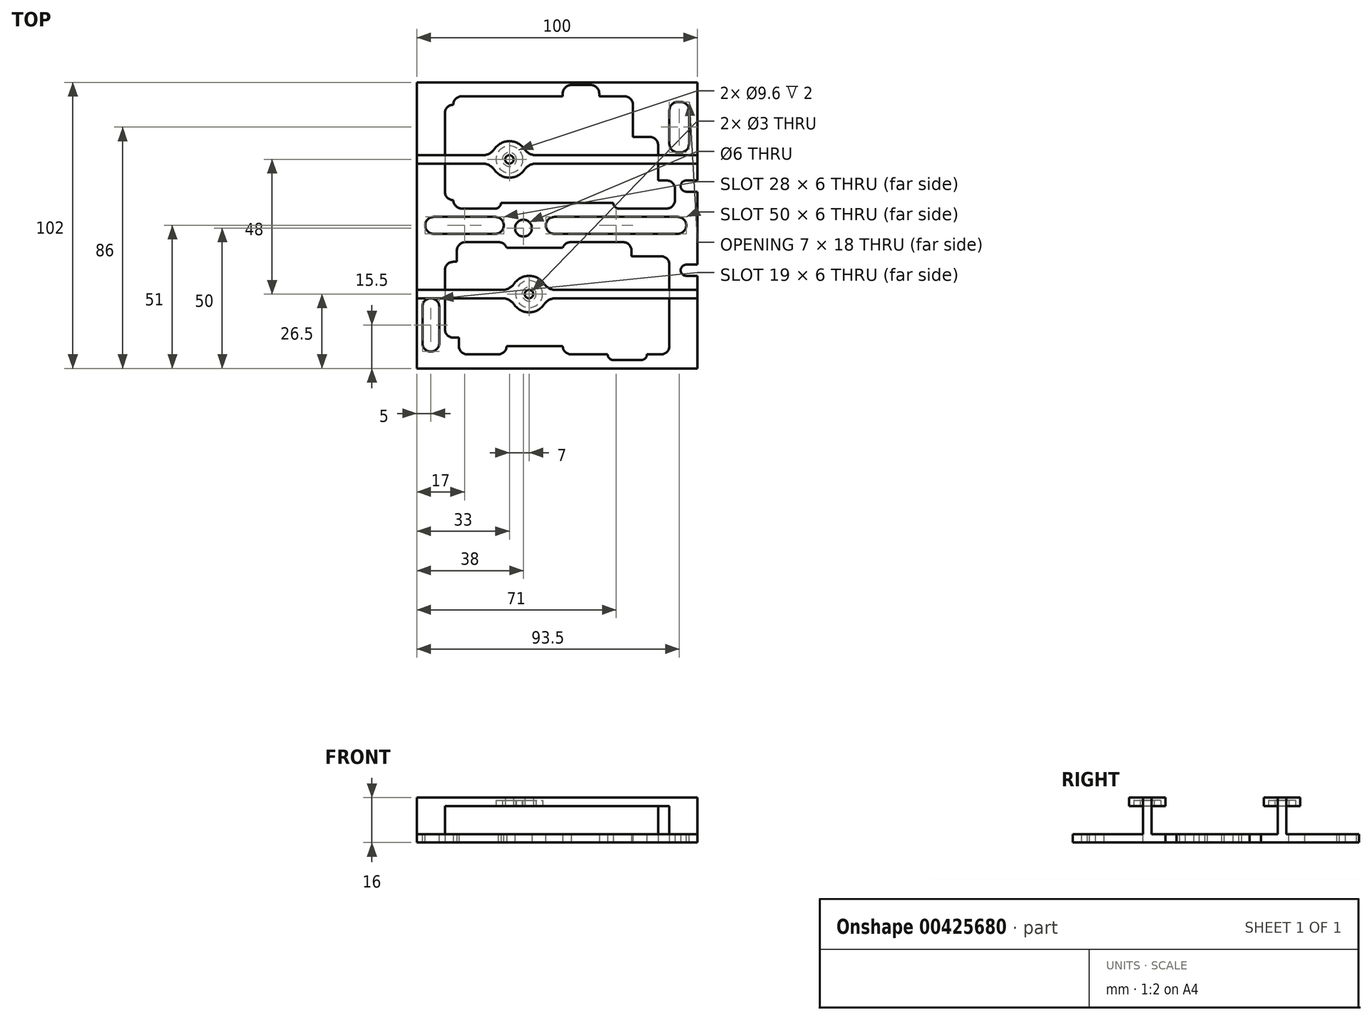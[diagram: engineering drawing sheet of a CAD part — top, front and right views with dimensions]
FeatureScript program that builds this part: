
annotation { "Feature Type Name" : "Feature", "Feature Type Description" : "" }
export const myFeature = defineFeature(function(context is Context, id is Id, definition is map)
    precondition{}
    {
        {
            var Q0;
            Q0=qCreatedBy(makeId("Top.planeOp"),FACE);
            var sketch = newSketch(context, id + "F0", { "sketchPlane" : qUnion([Q0])});
            skLineSegment(sketch, "E0.bottom", {"start": v(3, 0) * mm, "end": v(97, 0) * mm});
            skLineSegment(sketch, "E0.top", {"start": v(3, 102) * mm, "end": v(97, 102) * mm});
            skLineSegment(sketch, "E0.left", {"start": v(0, 0) * mm, "end": v(0, 102) * mm});
            skLineSegment(sketch, "E0.right", {"start": v(100, 0) * mm, "end": v(100, 33) * mm});
            skLineSegment(sketch, "E1.bottom", {"start": v(26, 97) * mm, "end": v(52, 97) * mm});
            skLineSegment(sketch, "E1.top", {"start": v(23, 57) * mm, "end": v(28, 57) * mm});
            skLineSegment(sketch, "E1.left", {"start": v(10, 91) * mm, "end": v(10, 63) * mm});
            skLineSegment(sketch, "E1.right", {"start": v(86, 79.5) * mm, "end": v(86, 67) * mm});
            skLineSegment(sketch, "E2.left", {"start": v(10, 35) * mm, "end": v(10, 14) * mm});
            skLineSegment(sketch, "E3.top", {"start": v(77, 82.5) * mm, "end": v(83, 82.5) * mm});
            skLineSegment(sketch, "E3.left", {"start": v(77, 88.5) * mm, "end": v(77, 82.5) * mm});
            skPoint(sketch, "E4.orphan", {"position": v(91.75, 82.5) * mm});
            skLineSegment(sketch, "E5.bottom", {"start": v(55, 101) * mm, "end": v(62, 101) * mm});
            skLineSegment(sketch, "E5.left", {"start": v(52, 98) * mm, "end": v(52, 97) * mm});
            skLineSegment(sketch, "E5.right", {"start": v(65, 98) * mm, "end": v(65, 97) * mm});
            skLineSegment(sketch, "E6.trimOffspring", {"start": v(65, 97) * mm, "end": v(74, 97) * mm});
            skLineSegment(sketch, "E7", {"start": v(72, 57) * mm, "end": v(89, 57) * mm});
            skLineSegment(sketch, "E8", {"start": v(86, 67) * mm, "end": v(89, 67) * mm});
            skLineSegment(sketch, "E9", {"start": v(92, 60) * mm, "end": v(92, 64) * mm});
            skLineSegment(sketch, "E10.top", {"start": v(14.3, 38) * mm, "end": v(13, 38) * mm});
            skLineSegment(sketch, "E11.bottom", {"start": v(13, 11) * mm, "end": v(15, 11) * mm});
            skLineSegment(sketch, "E12.trimOffspring", {"start": v(26, 45) * mm, "end": v(29.34, 45) * mm});
            skLineSegment(sketch, "E13.trimOffspring", {"start": v(24, 5) * mm, "end": v(29, 5) * mm});
            skLineSegment(sketch, "E14.right", {"start": v(90, 35.75) * mm, "end": v(90, 16.5) * mm});
            skLineSegment(sketch, "E15.top", {"start": v(70, 3) * mm, "end": v(80, 3) * mm});
            skLineSegment(sketch, "E16.trimOffspring", {"start": v(82, 5) * mm, "end": v(87, 5) * mm});
            skLineSegment(sketch, "E17", {"start": v(11.68, 51) * mm, "end": v(-20.94, 51) * mm, "construction": true});
            skCircle(sketch, "E18", {"center": v(38, 50) * mm, "radius": 3 * mm});
            skLineSegment(sketch, "E19", {"start": v(77, 88.5) * mm, "end": v(77, 94) * mm});
            skLineSegment(sketch, "E20", {"start": v(13, 94) * mm, "end": v(13, 94) * mm});
            skLineSegment(sketch, "E21", {"start": v(13, 60) * mm, "end": v(13, 60) * mm});
            skLineSegment(sketch, "E22", {"start": v(30, 59) * mm, "end": v(30, 59) * mm});
            skLineSegment(sketch, "E23", {"start": v(70, 59) * mm, "end": v(70, 59) * mm});
            skLineSegment(sketch, "E24", {"start": v(30, 59) * mm, "end": v(70, 59) * mm});
            skLineSegment(sketch, "E25", {"start": v(90, 16.5) * mm, "end": v(90, 8) * mm});
            skLineSegment(sketch, "E26", {"start": v(76.5, 42) * mm, "end": v(76.5, 40) * mm});
            skLineSegment(sketch, "E27", {"start": v(76.5, 40) * mm, "end": v(76.5, 40) * mm});
            skLineSegment(sketch, "E28.top", {"start": v(32, 8) * mm, "end": v(52, 8) * mm});
            skLineSegment(sketch, "E28.left", {"start": v(32, 8) * mm, "end": v(32, 8) * mm});
            skLineSegment(sketch, "E28.right", {"start": v(52, 8) * mm, "end": v(52, 8) * mm});
            skLineSegment(sketch, "E29.top", {"start": v(32, 43) * mm, "end": v(52, 43) * mm});
            skLineSegment(sketch, "E30.trimOffspring", {"start": v(55, 5) * mm, "end": v(68, 5) * mm});
            skLineSegment(sketch, "E31.trimOffspring", {"start": v(55, 45) * mm, "end": v(73.5, 45) * mm});
            skLineSegment(sketch, "E32", {"start": v(3, 0) * mm, "end": v(0, 0) * mm});
            skLineSegment(sketch, "E33", {"start": v(97, 0) * mm, "end": v(100, 0) * mm});
            skLineSegment(sketch, "E34", {"start": v(3, 102) * mm, "end": v(0, 102) * mm});
            skLineSegment(sketch, "E35", {"start": v(97, 102) * mm, "end": v(100, 102) * mm});
            skPoint(sketch, "E36.MirrorCS.start.orphan", {"position": v(100, 102) * mm});
            skLineSegment(sketch, "E37", {"start": v(26, 45) * mm, "end": v(17.3, 45) * mm});
            skLineSegment(sketch, "E38", {"start": v(14.3, 42) * mm, "end": v(14.3, 38) * mm});
            skArc(sketch, "E39.filletArc", {"start": v(17.3, 45) * mm, "mid": v(15.18, 44.12) * mm, "end": v(14.3, 42) * mm});
            skPoint(sketch, "E40.visualSharp", {"position": v(10, 38) * mm});
            skArc(sketch, "E40.filletArc", {"start": v(13, 38) * mm, "mid": v(10.88, 37.12) * mm, "end": v(10, 35) * mm});
            skPoint(sketch, "E41.visualSharp", {"position": v(10, 11) * mm});
            skArc(sketch, "E41.filletArc", {"start": v(10, 14) * mm, "mid": v(10.88, 11.88) * mm, "end": v(13, 11) * mm});
            skArc(sketch, "E42.filletArc", {"start": v(76.5, 42) * mm, "mid": v(75.62, 44.12) * mm, "end": v(73.5, 45) * mm});
            skLineSegment(sketch, "E43", {"start": v(76.5, 40) * mm, "end": v(87, 40) * mm});
            skLineSegment(sketch, "E44", {"start": v(90, 37) * mm, "end": v(90, 35.75) * mm});
            skPoint(sketch, "E45.visualSharp", {"position": v(90, 40) * mm});
            skArc(sketch, "E45.filletArc", {"start": v(90, 37) * mm, "mid": v(89.12, 39.12) * mm, "end": v(87, 40) * mm});
            skPoint(sketch, "E46.visualSharp", {"position": v(90, 5) * mm});
            skArc(sketch, "E46.filletArc", {"start": v(87, 5) * mm, "mid": v(89.12, 5.88) * mm, "end": v(90, 8) * mm});
            skPoint(sketch, "E47.visualSharp", {"position": v(52, 5) * mm});
            skArc(sketch, "E47.filletArc", {"start": v(52, 8) * mm, "mid": v(52.88, 5.88) * mm, "end": v(55, 5) * mm});
            skPoint(sketch, "E48.visualSharp", {"position": v(32, 5) * mm});
            skArc(sketch, "E48.filletArc", {"start": v(29, 5) * mm, "mid": v(31.12, 5.88) * mm, "end": v(32, 8) * mm});
            skArc(sketch, "E49", {"start": v(32, 43) * mm, "mid": v(30.83, 44.5) * mm, "end": v(29, 45) * mm});
            skPoint(sketch, "E29.left.start.orphan", {"position": v(32, 45) * mm});
            skArc(sketch, "E50", {"start": v(55, 45) * mm, "mid": v(53.17, 44.5) * mm, "end": v(52, 43) * mm});
            skArc(sketch, "E51", {"start": v(68, 5) * mm, "mid": v(68.59, 3.59) * mm, "end": v(70, 3) * mm});
            skArc(sketch, "E52", {"start": v(80, 3) * mm, "mid": v(81.41, 3.59) * mm, "end": v(82, 5) * mm});
            skLineSegment(sketch, "E53", {"start": v(18, 5) * mm, "end": v(24, 5) * mm});
            skLineSegment(sketch, "E54", {"start": v(15, 11) * mm, "end": v(15, 8) * mm});
            skPoint(sketch, "E55.visualSharp", {"position": v(15, 5) * mm});
            skArc(sketch, "E55.filletArc", {"start": v(15, 8) * mm, "mid": v(15.88, 5.88) * mm, "end": v(18, 5) * mm});
            skPoint(sketch, "E56.visualSharp", {"position": v(52, 101) * mm});
            skArc(sketch, "E56.filletArc", {"start": v(55, 101) * mm, "mid": v(52.88, 100.12) * mm, "end": v(52, 98) * mm});
            skPoint(sketch, "E57.visualSharp", {"position": v(65, 101) * mm});
            skArc(sketch, "E57.filletArc", {"start": v(65, 98) * mm, "mid": v(64.12, 100.12) * mm, "end": v(62, 101) * mm});
            skPoint(sketch, "E58.visualSharp", {"position": v(77, 97) * mm});
            skArc(sketch, "E58.filletArc", {"start": v(77, 94) * mm, "mid": v(76.12, 96.12) * mm, "end": v(74, 97) * mm});
            skPoint(sketch, "E59.visualSharp", {"position": v(86, 82.5) * mm});
            skArc(sketch, "E59.filletArc", {"start": v(86, 79.5) * mm, "mid": v(85.12, 81.62) * mm, "end": v(83, 82.5) * mm});
            skPoint(sketch, "E60.visualSharp", {"position": v(92, 67) * mm});
            skArc(sketch, "E60.filletArc", {"start": v(92, 64) * mm, "mid": v(91.12, 66.12) * mm, "end": v(89, 67) * mm});
            skPoint(sketch, "E61.visualSharp", {"position": v(92, 57) * mm});
            skArc(sketch, "E61.filletArc", {"start": v(89, 57) * mm, "mid": v(91.12, 57.88) * mm, "end": v(92, 60) * mm});
            skPoint(sketch, "E62.visualSharp", {"position": v(30, 57) * mm});
            skArc(sketch, "E62.filletArc", {"start": v(28, 57) * mm, "mid": v(29.41, 57.59) * mm, "end": v(30, 59) * mm});
            skPoint(sketch, "E63.visualSharp", {"position": v(70, 57) * mm});
            skArc(sketch, "E63.filletArc", {"start": v(70, 59) * mm, "mid": v(70.59, 57.59) * mm, "end": v(72, 57) * mm});
            skLineSegment(sketch, "E64", {"start": v(26, 97) * mm, "end": v(16, 97) * mm});
            skPoint(sketch, "E65.newPointA", {"position": v(13, 96.86) * mm});
            skPoint(sketch, "E65.newPointB", {"position": v(13, 97) * mm});
            skArc(sketch, "E65.filletArc", {"start": v(16, 97) * mm, "mid": v(13.88, 96.12) * mm, "end": v(13, 94) * mm});
            skPoint(sketch, "E66.visualSharp", {"position": v(10, 94) * mm});
            skArc(sketch, "E66.filletArc", {"start": v(13, 94) * mm, "mid": v(10.88, 93.12) * mm, "end": v(10, 91) * mm});
            skLineSegment(sketch, "E67", {"start": v(23, 57) * mm, "end": v(16, 57) * mm});
            skPoint(sketch, "E68.visualSharp", {"position": v(10, 60) * mm});
            skArc(sketch, "E68.filletArc", {"start": v(10, 63) * mm, "mid": v(10.88, 60.88) * mm, "end": v(13, 60) * mm});
            skPoint(sketch, "E69.visualSharp", {"position": v(13, 57) * mm});
            skArc(sketch, "E69.filletArc", {"start": v(13, 60) * mm, "mid": v(13.88, 57.88) * mm, "end": v(16, 57) * mm});
            skArc(sketch, "E70", {"start": v(96, 37) * mm, "mid": v(94, 35) * mm, "end": v(96, 33) * mm});
            skArc(sketch, "E71", {"start": v(96, 67) * mm, "mid": v(94, 65) * mm, "end": v(96, 63) * mm});
            skLineSegment(sketch, "E72", {"start": v(96, 67) * mm, "end": v(100, 67) * mm});
            skLineSegment(sketch, "E73", {"start": v(96, 63) * mm, "end": v(100, 63) * mm});
            skLineSegment(sketch, "E74.trimOffspring", {"start": v(100, 67) * mm, "end": v(100, 102) * mm});
            skLineSegment(sketch, "E75.bottom", {"start": v(96, 37) * mm, "end": v(100, 37) * mm});
            skLineSegment(sketch, "E76.bottom", {"start": v(96, 33) * mm, "end": v(100, 33) * mm});
            skLineSegment(sketch, "E77.trimOffspring", {"start": v(100, 37) * mm, "end": v(100, 63) * mm});
            skSolve(sketch);
        }
        {
            var Q0;
            Q0=qSketchRegion(id+"F0",true);
            extrude(context, id + "F1", {"entities" : qUnion([Q0]), "depth" : 3 * mm, "offsetDistance" : 25 * mm});
        }
        {
            var Q0;
            Q0=makeQuery(id+"F1.opExtrude","CAP_FACE",FACE,{"disambiguationData":[OSD([sQuery(id+"F0.wireOp",EDGE,"E0.bottom"),sQuery(id+"F0.wireOp",EDGE,"E0.top"),sQuery(id+"F0.wireOp",EDGE,"E0.left"),sQuery(id+"F0.wireOp",EDGE,"E0.right"),sQuery(id+"F0.wireOp",EDGE,"E1.bottom"),sQuery(id+"F0.wireOp",EDGE,"E1.top"),sQuery(id+"F0.wireOp",EDGE,"E1.left"),sQuery(id+"F0.wireOp",EDGE,"E1.right"),sQuery(id+"F0.wireOp",EDGE,"E2.left"),sQuery(id+"F0.wireOp",EDGE,"E2.right"),sQuery(id+"F0.wireOp",EDGE,"E3.top"),sQuery(id+"F0.wireOp",EDGE,"E3.left"),sQuery(id+"F0.wireOp",EDGE,"E5.bottom"),sQuery(id+"F0.wireOp",EDGE,"E5.left"),sQuery(id+"F0.wireOp",EDGE,"E5.right"),sQuery(id+"F0.wireOp",EDGE,"E6.trimOffspring"),sQuery(id+"F0.wireOp",EDGE,"OxCn24rm-5nCi-klrK-E0W5-i8LOYMI6os4h.bottom"),sQuery(id+"F0.wireOp",EDGE,"OxCn24rm-5nCi-klrK-E0W5-i8LOYMI6os4h.right"),sQuery(id+"F0.wireOp",EDGE,"rXKhr1xD-5eTB-sLtH-Qrwl-SqILkHBMoKIC.top"),sQuery(id+"F0.wireOp",EDGE,"rXKhr1xD-5eTB-sLtH-Qrwl-SqILkHBMoKIC.right"),sQuery(id+"F0.wireOp",EDGE,"wjIKWsUY-1y7m-uhNO-1cWs-wJh5i1SVGTS4"),sQuery(id+"F0.wireOp",EDGE,"Fd2FQQkF-qeS2-SP9m-kDKw-uxav5DLLBaqb"),sQuery(id+"F0.wireOp",EDGE,"ZQqpw7ko-XBrV-Zwog-WddX-ZsBwI7n4kIzG"),sQuery(id+"F0.wireOp",EDGE,"E7"),sQuery(id+"F0.wireOp",EDGE,"E8"),sQuery(id+"F0.wireOp",EDGE,"E9"),sQuery(id+"F0.wireOp",EDGE,"ORbpDnOW-ThUp-Z5K2-SE26-eshPCraVd0tb.top"),sQuery(id+"F0.wireOp",EDGE,"ORbpDnOW-ThUp-Z5K2-SE26-eshPCraVd0tb.left"),sQuery(id+"F0.wireOp",EDGE,"E10.top"),sQuery(id+"F0.wireOp",EDGE,"E10.left"),sQuery(id+"F0.wireOp",EDGE,"dN3iFH4H-qRAM-YeRZ-ol0c-A4IXgtGxA8XV.top"),sQuery(id+"F0.wireOp",EDGE,"dN3iFH4H-qRAM-YeRZ-ol0c-A4IXgtGxA8XV.left"),sQuery(id+"F0.wireOp",EDGE,"E11.bottom"),sQuery(id+"F0.wireOp",EDGE,"E11.right"),sQuery(id+"F0.wireOp",EDGE,"E12.trimOffspring"),sQuery(id+"F0.wireOp",EDGE,"E13.trimOffspring"),sQuery(id+"F0.wireOp",EDGE,"bjdKxRGc-RBqR-6Ud0-CWuA-04plJlh88Ydx.top"),sQuery(id+"F0.wireOp",EDGE,"bjdKxRGc-RBqR-6Ud0-CWuA-04plJlh88Ydx.left"),sQuery(id+"F0.wireOp",EDGE,"E14.right"),sQuery(id+"F0.wireOp",EDGE,"2f8da56e-dfad-408c-ba04-36b25fe1f5d9.trimOffspring"),sQuery(id+"F0.wireOp",EDGE,"E15.top"),sQuery(id+"F0.wireOp",EDGE,"E15.left"),sQuery(id+"F0.wireOp",EDGE,"E15.right"),sQuery(id+"F0.wireOp",EDGE,"E16.trimOffspring"),sQuery(id+"F0.wireOp",EDGE,"A49D6E9r-1JUr-9GDP-vNaZ-ViviVAoOX606"),sQuery(id+"F0.wireOp",EDGE,"vtlNYRCa-Do6P-C0d5-ElFE-HTToTMsx1Fji"),sQuery(id+"F0.wireOp",EDGE,"lmL8inpJ-ytwe-dLrc-ad7L-TpwxuQ8vTU9b"),sQuery(id+"F0.wireOp",EDGE,"h73Oo6xC-rRRI-xAcJ-BuA6-SMJPpPIosUSZ"),sQuery(id+"F0.wireOp",EDGE,"au1NNZ2t-6lUs-IFa9-xlba-gWE9ZIKOgp08"),sQuery(id+"F0.wireOp",EDGE,"yvoELJC3-YjSa-WHdH-b68Q-IG7KWKIGRjHb"),sQuery(id+"F0.wireOp",EDGE,"ERycc8vl-z3Cl-hGIG-RQzm-87voCwp2birA"),sQuery(id+"F0.wireOp",EDGE,"E2MXITla-3G0j-ucNW-0Zkd-STVuzueoCgdE.top"),sQuery(id+"F0.wireOp",EDGE,"E2MXITla-3G0j-ucNW-0Zkd-STVuzueoCgdE.left"),sQuery(id+"F0.wireOp",EDGE,"E2MXITla-3G0j-ucNW-0Zkd-STVuzueoCgdE.right"),sQuery(id+"F0.wireOp",EDGE,"Ca3rMzd9-FrgB-pphp-Oxqs-IZKiP3cJTDne"),sQuery(id+"F0.wireOp",EDGE,"7T3Rpf4S-CqYs-le4C-O5dJ-dI1EBJDtCbfp"),sQuery(id+"F0.wireOp",EDGE,"997c3999-b55e-490c-beb5-2bee1e2e1c940.MirrorCS"),sQuery(id+"F0.wireOp",EDGE,"c3554b98-e3f3-445f-801e-a0076f2162810.MirrorCS"),sQuery(id+"F0.wireOp",EDGE,"E36.MirrorCS"),sQuery(id+"F0.wireOp",EDGE,"4368e434-94b6-4df4-879f-dcd640d41f0e0.MirrorCS"),sQuery(id+"F0.wireOp",EDGE,"37798aaa-42c0-4cef-a439-54f5e668db9a0.MirrorCS"),sQuery(id+"F0.wireOp",EDGE,"d064ad95-df91-4078-a0f9-9f58f394fbd70.MirrorCS"),sQuery(id+"F0.wireOp",EDGE,"08820286-3d7b-404e-9f5a-cb54356c3d8d0.MirrorCS"),sQuery(id+"F0.wireOp",EDGE,"1518c572-78e2-41d5-bc5d-d8ca2dcde2710.MirrorCS"),sQuery(id+"F0.wireOp",EDGE,"E18"),sQuery(id+"F0.wireOp",EDGE,"DqYHB80w-fGch-NoDe-N2a7-YfNS9cl1PrHZ"),sQuery(id+"F0.wireOp",EDGE,"Tbt3sgnV-WqdU-Oisj-Q5Qw-zABe9o91ZCy5"),sQuery(id+"F0.wireOp",EDGE,"fXqGHVZl-Qcgk-zm2a-7tLV-AyFcCwGseMAn"),sQuery(id+"F0.wireOp",EDGE,"RIbojJIC-BDsi-60La-0oJR-OISrQjfgBfsT"),sQuery(id+"F0.wireOp",EDGE,"Y7Jcioam-hEoO-QEPg-HWFz-VR7Pjhn3heaJ"),sQuery(id+"F0.wireOp",EDGE,"PzUnhAa5-5pe3-GNiC-2A5K-FJAJxwR9T3X4"),sQuery(id+"F0.wireOp",EDGE,"rlzUklQd-3dkf-QKTa-yDw8-YwjNvcUjzYi0"),sQuery(id+"F0.wireOp",EDGE,"JA5SAORn-5zCI-tt9o-vuvb-NJhDItHEi9iq"),sQuery(id+"F0.wireOp",EDGE,"qvz8dSCR-gKGT-wn8P-gyaW-mG4SNKuXNP92"),sQuery(id+"F0.wireOp",EDGE,"Ehq0zpWA-Svbj-95kT-JLI7-XYxp3DV2qt0l")])],"isStart":false});
            var sketch = newSketch(context, id + "F2", { "sketchPlane" : qUnion([Q0])});
            skLineSegment(sketch, "E78.bottom", {"start": v(0, 25) * mm, "end": v(10, 25) * mm});
            skLineSegment(sketch, "E78.top", {"start": v(0, 28) * mm, "end": v(10, 28) * mm});
            skLineSegment(sketch, "E78.left", {"start": v(0, 25) * mm, "end": v(0, 28) * mm});
            skLineSegment(sketch, "E78.right", {"start": v(100, 25) * mm, "end": v(100, 28) * mm});
            skLineSegment(sketch, "E79.bottom", {"start": v(0, 73) * mm, "end": v(10, 73) * mm});
            skLineSegment(sketch, "E79.top", {"start": v(0, 76) * mm, "end": v(10, 76) * mm});
            skLineSegment(sketch, "E79.left", {"start": v(0, 73) * mm, "end": v(0, 76) * mm});
            skLineSegment(sketch, "E79.right", {"start": v(100, 73) * mm, "end": v(100, 76) * mm});
            skLineSegment(sketch, "E80", {"start": v(10, 73) * mm, "end": v(10, 76) * mm});
            skLineSegment(sketch, "E81", {"start": v(10, 28) * mm, "end": v(10, 25) * mm});
            skLineSegment(sketch, "E82", {"start": v(90, 28) * mm, "end": v(90, 25) * mm});
            skLineSegment(sketch, "E83", {"start": v(86, 76) * mm, "end": v(86, 73) * mm});
            skLineSegment(sketch, "E84.trimOffspring", {"start": v(90, 28) * mm, "end": v(100, 28) * mm});
            skLineSegment(sketch, "E85.trimOffspring", {"start": v(90, 25) * mm, "end": v(100, 25) * mm});
            skLineSegment(sketch, "E86.trimOffspring", {"start": v(86, 76) * mm, "end": v(100, 76) * mm});
            skLineSegment(sketch, "E87.trimOffspring", {"start": v(86, 73) * mm, "end": v(100, 73) * mm});
            skSolve(sketch);
        }
        {
            var Q0;
            Q0=qSketchRegion(id+"F2",true);
            extrude(context, id + "F3", {"entities" : qUnion([Q0]), "operationType" : NewBodyOperationType.ADD, "depth" : 10 * mm});
        }
        {
            var Q0;
            Q0=makeQuery(id+"F3.opExtrude","CAP_FACE",FACE,{"disambiguationData":[OSD([sQuery(id+"F2.wireOp",EDGE,"E78.bottom"),sQuery(id+"F2.wireOp",EDGE,"E78.top"),sQuery(id+"F2.wireOp",EDGE,"E78.left"),sQuery(id+"F2.wireOp",EDGE,"E81")])],"isStart":false});
            var sketch = newSketch(context, id + "F4", { "sketchPlane" : qUnion([Q0])});
            skLineSegment(sketch, "E88.0", {"start": v(0, 25) * mm, "end": v(0, 28) * mm});
            skLineSegment(sketch, "E89.0", {"start": v(100, 28) * mm, "end": v(100, 25) * mm});
            skLineSegment(sketch, "E90.0", {"start": v(100, 76) * mm, "end": v(100, 73) * mm});
            skLineSegment(sketch, "E91.0", {"start": v(0, 73) * mm, "end": v(0, 76) * mm});
            skLineSegment(sketch, "E92", {"start": v(0, 76) * mm, "end": v(26.68, 76) * mm});
            skLineSegment(sketch, "E93", {"start": v(0, 73) * mm, "end": v(26.68, 73) * mm});
            skLineSegment(sketch, "E94", {"start": v(0, 28) * mm, "end": v(33.68, 28) * mm});
            skLineSegment(sketch, "E95", {"start": v(0, 25) * mm, "end": v(33.68, 25) * mm});
            skArc(sketch, "E96", {"start": v(26.68, 73) * mm, "mid": v(33, 68) * mm, "end": v(39.32, 73) * mm});
            skArc(sketch, "E97", {"start": v(33.68, 25) * mm, "mid": v(40, 20) * mm, "end": v(46.32, 25) * mm});
            skLineSegment(sketch, "E98.trimOffspring", {"start": v(39.32, 73) * mm, "end": v(100, 73) * mm});
            skLineSegment(sketch, "E99.trimOffspring", {"start": v(39.32, 76) * mm, "end": v(100, 76) * mm});
            skArc(sketch, "E100.trimOffspring", {"start": v(39.32, 76) * mm, "mid": v(33, 81) * mm, "end": v(26.68, 76) * mm});
            skLineSegment(sketch, "E101.trimOffspring", {"start": v(46.32, 28) * mm, "end": v(100, 28) * mm});
            skLineSegment(sketch, "E102.trimOffspring", {"start": v(46.32, 25) * mm, "end": v(100, 25) * mm});
            skArc(sketch, "E103.trimOffspring", {"start": v(46.32, 28) * mm, "mid": v(40, 33) * mm, "end": v(33.68, 28) * mm});
            skSolve(sketch);
        }
        {
            var Q0;
            Q0 = qSketchRegion(id + "F4", true);
            extrude(context, id + "F5", {"entities" : qUnion([Q0]), "operationType" : NewBodyOperationType.ADD, "depth" : 3 * mm});
        }
        {
            var Q0;
            Q0=makeQuery(id+"F5.opExtrude","CAP_FACE",FACE,{"disambiguationData":[OSD([sQuery(id+"F4.wireOp",EDGE,"E88.0"),sQuery(id+"F4.wireOp",EDGE,"E89.0"),sQuery(id+"F4.wireOp",EDGE,"E94"),sQuery(id+"F4.wireOp",EDGE,"E95"),sQuery(id+"F4.wireOp",EDGE,"E97"),sQuery(id+"F4.wireOp",EDGE,"E101.trimOffspring"),sQuery(id+"F4.wireOp",EDGE,"E102.trimOffspring"),sQuery(id+"F4.wireOp",EDGE,"E103.trimOffspring")])],"isStart":true});
            var sketch = newSketch(context, id + "F6", { "sketchPlane" : qUnion([Q0])});
            skCircle(sketch, "E104", {"center": v(40, -26.5) * mm, "radius": 4.8 * mm});
            skCircle(sketch, "E105", {"center": v(33, -74.5) * mm, "radius": 4.8 * mm});
            skCircle(sketch, "E106", {"center": v(40, -26.5) * mm, "radius": 2.5 * mm});
            skCircle(sketch, "E107", {"center": v(33, -74.5) * mm, "radius": 2.5 * mm});
            skSolve(sketch);
        }
        {
            var Q0;
            Q0 = qSketchRegion(id + "F6", true);
            extrude(context, id + "F7", {"entities" : qUnion([Q0]), "operationType" : NewBodyOperationType.REMOVE, "oppositeDirection" : true, "depth" : 2 * mm});
        }
        {
            var Q0;
            Q0=makeQuery(id+"F1.opExtrude","CAP_FACE",FACE,{"disambiguationData":[OSD([sQuery(id+"F0.wireOp",EDGE,"E0.bottom"),sQuery(id+"F0.wireOp",EDGE,"E0.top"),sQuery(id+"F0.wireOp",EDGE,"E0.left"),sQuery(id+"F0.wireOp",EDGE,"E0.right"),sQuery(id+"F0.wireOp",EDGE,"E1.bottom"),sQuery(id+"F0.wireOp",EDGE,"E1.top"),sQuery(id+"F0.wireOp",EDGE,"E1.left"),sQuery(id+"F0.wireOp",EDGE,"E1.right"),sQuery(id+"F0.wireOp",EDGE,"E2.left"),sQuery(id+"F0.wireOp",EDGE,"E2.right"),sQuery(id+"F0.wireOp",EDGE,"E3.top"),sQuery(id+"F0.wireOp",EDGE,"E3.left"),sQuery(id+"F0.wireOp",EDGE,"E5.bottom"),sQuery(id+"F0.wireOp",EDGE,"E5.left"),sQuery(id+"F0.wireOp",EDGE,"E5.right"),sQuery(id+"F0.wireOp",EDGE,"E6.trimOffspring"),sQuery(id+"F0.wireOp",EDGE,"OxCn24rm-5nCi-klrK-E0W5-i8LOYMI6os4h.bottom"),sQuery(id+"F0.wireOp",EDGE,"OxCn24rm-5nCi-klrK-E0W5-i8LOYMI6os4h.right"),sQuery(id+"F0.wireOp",EDGE,"rXKhr1xD-5eTB-sLtH-Qrwl-SqILkHBMoKIC.top"),sQuery(id+"F0.wireOp",EDGE,"rXKhr1xD-5eTB-sLtH-Qrwl-SqILkHBMoKIC.right"),sQuery(id+"F0.wireOp",EDGE,"wjIKWsUY-1y7m-uhNO-1cWs-wJh5i1SVGTS4"),sQuery(id+"F0.wireOp",EDGE,"Fd2FQQkF-qeS2-SP9m-kDKw-uxav5DLLBaqb"),sQuery(id+"F0.wireOp",EDGE,"ZQqpw7ko-XBrV-Zwog-WddX-ZsBwI7n4kIzG"),sQuery(id+"F0.wireOp",EDGE,"E7"),sQuery(id+"F0.wireOp",EDGE,"E8"),sQuery(id+"F0.wireOp",EDGE,"E9"),sQuery(id+"F0.wireOp",EDGE,"ORbpDnOW-ThUp-Z5K2-SE26-eshPCraVd0tb.top"),sQuery(id+"F0.wireOp",EDGE,"ORbpDnOW-ThUp-Z5K2-SE26-eshPCraVd0tb.left"),sQuery(id+"F0.wireOp",EDGE,"E10.top"),sQuery(id+"F0.wireOp",EDGE,"E10.left"),sQuery(id+"F0.wireOp",EDGE,"dN3iFH4H-qRAM-YeRZ-ol0c-A4IXgtGxA8XV.top"),sQuery(id+"F0.wireOp",EDGE,"dN3iFH4H-qRAM-YeRZ-ol0c-A4IXgtGxA8XV.left"),sQuery(id+"F0.wireOp",EDGE,"E11.bottom"),sQuery(id+"F0.wireOp",EDGE,"E11.right"),sQuery(id+"F0.wireOp",EDGE,"E12.trimOffspring"),sQuery(id+"F0.wireOp",EDGE,"E13.trimOffspring"),sQuery(id+"F0.wireOp",EDGE,"bjdKxRGc-RBqR-6Ud0-CWuA-04plJlh88Ydx.top"),sQuery(id+"F0.wireOp",EDGE,"bjdKxRGc-RBqR-6Ud0-CWuA-04plJlh88Ydx.left"),sQuery(id+"F0.wireOp",EDGE,"E14.right"),sQuery(id+"F0.wireOp",EDGE,"2f8da56e-dfad-408c-ba04-36b25fe1f5d9.trimOffspring"),sQuery(id+"F0.wireOp",EDGE,"E15.top"),sQuery(id+"F0.wireOp",EDGE,"E15.left"),sQuery(id+"F0.wireOp",EDGE,"E15.right"),sQuery(id+"F0.wireOp",EDGE,"E16.trimOffspring"),sQuery(id+"F0.wireOp",EDGE,"A49D6E9r-1JUr-9GDP-vNaZ-ViviVAoOX606"),sQuery(id+"F0.wireOp",EDGE,"vtlNYRCa-Do6P-C0d5-ElFE-HTToTMsx1Fji"),sQuery(id+"F0.wireOp",EDGE,"lmL8inpJ-ytwe-dLrc-ad7L-TpwxuQ8vTU9b"),sQuery(id+"F0.wireOp",EDGE,"h73Oo6xC-rRRI-xAcJ-BuA6-SMJPpPIosUSZ"),sQuery(id+"F0.wireOp",EDGE,"au1NNZ2t-6lUs-IFa9-xlba-gWE9ZIKOgp08"),sQuery(id+"F0.wireOp",EDGE,"yvoELJC3-YjSa-WHdH-b68Q-IG7KWKIGRjHb"),sQuery(id+"F0.wireOp",EDGE,"ERycc8vl-z3Cl-hGIG-RQzm-87voCwp2birA"),sQuery(id+"F0.wireOp",EDGE,"E2MXITla-3G0j-ucNW-0Zkd-STVuzueoCgdE.top"),sQuery(id+"F0.wireOp",EDGE,"E2MXITla-3G0j-ucNW-0Zkd-STVuzueoCgdE.left"),sQuery(id+"F0.wireOp",EDGE,"E2MXITla-3G0j-ucNW-0Zkd-STVuzueoCgdE.right"),sQuery(id+"F0.wireOp",EDGE,"Ca3rMzd9-FrgB-pphp-Oxqs-IZKiP3cJTDne"),sQuery(id+"F0.wireOp",EDGE,"7T3Rpf4S-CqYs-le4C-O5dJ-dI1EBJDtCbfp"),sQuery(id+"F0.wireOp",EDGE,"997c3999-b55e-490c-beb5-2bee1e2e1c940.MirrorCS"),sQuery(id+"F0.wireOp",EDGE,"c3554b98-e3f3-445f-801e-a0076f2162810.MirrorCS"),sQuery(id+"F0.wireOp",EDGE,"E36.MirrorCS"),sQuery(id+"F0.wireOp",EDGE,"4368e434-94b6-4df4-879f-dcd640d41f0e0.MirrorCS"),sQuery(id+"F0.wireOp",EDGE,"37798aaa-42c0-4cef-a439-54f5e668db9a0.MirrorCS"),sQuery(id+"F0.wireOp",EDGE,"d064ad95-df91-4078-a0f9-9f58f394fbd70.MirrorCS"),sQuery(id+"F0.wireOp",EDGE,"08820286-3d7b-404e-9f5a-cb54356c3d8d0.MirrorCS"),sQuery(id+"F0.wireOp",EDGE,"1518c572-78e2-41d5-bc5d-d8ca2dcde2710.MirrorCS"),sQuery(id+"F0.wireOp",EDGE,"E18"),sQuery(id+"F0.wireOp",EDGE,"DqYHB80w-fGch-NoDe-N2a7-YfNS9cl1PrHZ"),sQuery(id+"F0.wireOp",EDGE,"Tbt3sgnV-WqdU-Oisj-Q5Qw-zABe9o91ZCy5"),sQuery(id+"F0.wireOp",EDGE,"fXqGHVZl-Qcgk-zm2a-7tLV-AyFcCwGseMAn"),sQuery(id+"F0.wireOp",EDGE,"RIbojJIC-BDsi-60La-0oJR-OISrQjfgBfsT"),sQuery(id+"F0.wireOp",EDGE,"Y7Jcioam-hEoO-QEPg-HWFz-VR7Pjhn3heaJ"),sQuery(id+"F0.wireOp",EDGE,"PzUnhAa5-5pe3-GNiC-2A5K-FJAJxwR9T3X4"),sQuery(id+"F0.wireOp",EDGE,"rlzUklQd-3dkf-QKTa-yDw8-YwjNvcUjzYi0"),sQuery(id+"F0.wireOp",EDGE,"JA5SAORn-5zCI-tt9o-vuvb-NJhDItHEi9iq"),sQuery(id+"F0.wireOp",EDGE,"qvz8dSCR-gKGT-wn8P-gyaW-mG4SNKuXNP92"),sQuery(id+"F0.wireOp",EDGE,"Ehq0zpWA-Svbj-95kT-JLI7-XYxp3DV2qt0l")])],"isStart":false});
            var sketch = newSketch(context, id + "F8", { "sketchPlane" : qUnion([Q0])});
            skLineSegment(sketch, "E108.bottom", {"start": v(49, 54) * mm, "end": v(93, 54) * mm});
            skLineSegment(sketch, "E108.top", {"start": v(49, 48) * mm, "end": v(93, 48) * mm});
            skLineSegment(sketch, "E108.left", {"start": v(46, 51) * mm, "end": v(46, 51) * mm});
            skLineSegment(sketch, "E108.right", {"start": v(96, 51) * mm, "end": v(96, 51) * mm});
            skLineSegment(sketch, "E109.bottom", {"start": v(93, 77) * mm, "end": v(94, 77) * mm});
            skLineSegment(sketch, "E109.top", {"start": v(93, 95) * mm, "end": v(94, 95) * mm});
            skLineSegment(sketch, "E109.left", {"start": v(90, 80) * mm, "end": v(90, 92) * mm});
            skLineSegment(sketch, "E109.right", {"start": v(97, 80) * mm, "end": v(97, 92) * mm});
            skLineSegment(sketch, "E110.right", {"start": v(2, 9) * mm, "end": v(2, 22) * mm});
            skLineSegment(sketch, "E111.bottom", {"start": v(28, 54) * mm, "end": v(6, 54) * mm});
            skLineSegment(sketch, "E111.top", {"start": v(28, 48) * mm, "end": v(6, 48) * mm});
            skLineSegment(sketch, "E111.left", {"start": v(31, 51) * mm, "end": v(31, 51) * mm});
            skLineSegment(sketch, "E111.right", {"start": v(3, 51) * mm, "end": v(3, 51) * mm});
            skLineSegment(sketch, "E112", {"start": v(5, 6) * mm, "end": v(5, 6) * mm});
            skLineSegment(sketch, "E113", {"start": v(8, 9) * mm, "end": v(8, 22) * mm});
            skPoint(sketch, "E114.visualSharp", {"position": v(46, 54) * mm});
            skArc(sketch, "E114.filletArc", {"start": v(49, 54) * mm, "mid": v(46.88, 53.12) * mm, "end": v(46, 51) * mm});
            skPoint(sketch, "E115.visualSharp", {"position": v(46, 48) * mm});
            skArc(sketch, "E115.filletArc", {"start": v(46, 51) * mm, "mid": v(46.88, 48.88) * mm, "end": v(49, 48) * mm});
            skPoint(sketch, "E116.visualSharp", {"position": v(96, 54) * mm});
            skArc(sketch, "E116.filletArc", {"start": v(96, 51) * mm, "mid": v(95.12, 53.12) * mm, "end": v(93, 54) * mm});
            skPoint(sketch, "E117.visualSharp", {"position": v(96, 48) * mm});
            skArc(sketch, "E117.filletArc", {"start": v(93, 48) * mm, "mid": v(95.12, 48.88) * mm, "end": v(96, 51) * mm});
            skPoint(sketch, "E118.visualSharp", {"position": v(3, 54) * mm});
            skArc(sketch, "E118.filletArc", {"start": v(6, 54) * mm, "mid": v(3.88, 53.12) * mm, "end": v(3, 51) * mm});
            skPoint(sketch, "E119.visualSharp", {"position": v(3, 48) * mm});
            skArc(sketch, "E119.filletArc", {"start": v(3, 51) * mm, "mid": v(3.88, 48.88) * mm, "end": v(6, 48) * mm});
            skPoint(sketch, "E120.visualSharp", {"position": v(31, 54) * mm});
            skArc(sketch, "E120.filletArc", {"start": v(31, 51) * mm, "mid": v(30.12, 53.12) * mm, "end": v(28, 54) * mm});
            skPoint(sketch, "E121.visualSharp", {"position": v(31, 48) * mm});
            skArc(sketch, "E121.filletArc", {"start": v(28, 48) * mm, "mid": v(30.12, 48.88) * mm, "end": v(31, 51) * mm});
            skLineSegment(sketch, "E122", {"start": v(5, 25) * mm, "end": v(5, 25) * mm});
            skArc(sketch, "E123.filletArc", {"start": v(5, 25) * mm, "mid": v(2.88, 24.12) * mm, "end": v(2, 22) * mm});
            skArc(sketch, "E124.filletArc", {"start": v(8, 22) * mm, "mid": v(7.12, 24.12) * mm, "end": v(5, 25) * mm});
            skArc(sketch, "E125.filletArc", {"start": v(2, 9) * mm, "mid": v(2.88, 6.88) * mm, "end": v(5, 6) * mm});
            skArc(sketch, "E126.filletArc", {"start": v(5, 6) * mm, "mid": v(7.12, 6.88) * mm, "end": v(8, 9) * mm});
            skPoint(sketch, "E127.visualSharp", {"position": v(90, 77) * mm});
            skArc(sketch, "E127.filletArc", {"start": v(90, 80) * mm, "mid": v(90.88, 77.88) * mm, "end": v(93, 77) * mm});
            skPoint(sketch, "E128.visualSharp", {"position": v(97, 77) * mm});
            skArc(sketch, "E128.filletArc", {"start": v(94, 77) * mm, "mid": v(96.12, 77.88) * mm, "end": v(97, 80) * mm});
            skPoint(sketch, "E129.visualSharp", {"position": v(90, 95) * mm});
            skArc(sketch, "E129.filletArc", {"start": v(93, 95) * mm, "mid": v(90.88, 94.12) * mm, "end": v(90, 92) * mm});
            skPoint(sketch, "E130.visualSharp", {"position": v(97, 95) * mm});
            skArc(sketch, "E130.filletArc", {"start": v(97, 92) * mm, "mid": v(96.12, 94.12) * mm, "end": v(94, 95) * mm});
            skSolve(sketch);
        }
        {
            var Q0;
            Q0 = qSketchRegion(id + "F8", true);
            extrude(context, id + "F9", {"entities" : qUnion([Q0]), "operationType" : NewBodyOperationType.REMOVE, "oppositeDirection" : true, "depth" : 25 * mm});
        }
        {
            var Q0;
            Q0=makeQuery(id+"F5.opExtrude","SWEPT_EDGE",EDGE,{"disambiguationData":[OSD([sQuery(id+"F4.wireOp",EDGE,"E95"),sQuery(id+"F4.wireOp",EDGE,"E97")])]});
            var Q1;
            Q1=makeQuery(id+"F5.opExtrude","SWEPT_EDGE",EDGE,{"disambiguationData":[OSD([sQuery(id+"F4.wireOp",EDGE,"E97"),sQuery(id+"F4.wireOp",EDGE,"E102.trimOffspring")])]});
            var Q2;
            Q2=makeQuery(id+"F5.opExtrude","SWEPT_EDGE",EDGE,{"disambiguationData":[OSD([sQuery(id+"F4.wireOp",EDGE,"E101.trimOffspring"),sQuery(id+"F4.wireOp",EDGE,"E103.trimOffspring")])]});
            var Q3;
            Q3=makeQuery(id+"F5.opExtrude","SWEPT_EDGE",EDGE,{"disambiguationData":[OSD([sQuery(id+"F4.wireOp",EDGE,"E99.trimOffspring"),sQuery(id+"F4.wireOp",EDGE,"E100.trimOffspring")])]});
            var Q4;
            Q4=makeQuery(id+"F5.opExtrude","SWEPT_EDGE",EDGE,{"disambiguationData":[OSD([sQuery(id+"F4.wireOp",EDGE,"E94"),sQuery(id+"F4.wireOp",EDGE,"E103.trimOffspring")])]});
            var Q5;
            Q5=makeQuery(id+"F5.opExtrude","SWEPT_EDGE",EDGE,{"disambiguationData":[OSD([sQuery(id+"F4.wireOp",EDGE,"E92"),sQuery(id+"F4.wireOp",EDGE,"E100.trimOffspring")])]});
            var Q6;
            Q6=makeQuery(id+"F5.opExtrude","SWEPT_EDGE",EDGE,{"disambiguationData":[OSD([sQuery(id+"F4.wireOp",EDGE,"E93"),sQuery(id+"F4.wireOp",EDGE,"E96")])]});
            var Q7;
            Q7=makeQuery(id+"F5.opExtrude","SWEPT_EDGE",EDGE,{"disambiguationData":[OSD([sQuery(id+"F4.wireOp",EDGE,"E96"),sQuery(id+"F4.wireOp",EDGE,"E98.trimOffspring")])]});
            fillet(context, id + "F10", {"entities" : qUnion([Q0, Q1, Q2, Q3, Q4, Q5, Q6, Q7]), "radius" : 5 * mm, "tangentPropagation" : true, "allowEdgeOverflow" : false});
        }
        {
            var Q0;
            Q0=makeQuery(id+"F7.boolean.opBoolean","SPLIT",FACE,{"disambiguationData":[TD([makeQuery(id+"F7.opExtrude","SWEPT_FACE",FACE,{"disambiguationData":[OSD([sQuery(id+"F6.wireOp",EDGE,"E106")])]})])],"derivedFrom":makeQuery(id+"F5.opExtrude","CAP_FACE",FACE,{"disambiguationData":[OSD([sQuery(id+"F4.wireOp",EDGE,"E88.0"),sQuery(id+"F4.wireOp",EDGE,"E89.0"),sQuery(id+"F4.wireOp",EDGE,"E94"),sQuery(id+"F4.wireOp",EDGE,"E95"),sQuery(id+"F4.wireOp",EDGE,"E97"),sQuery(id+"F4.wireOp",EDGE,"E101.trimOffspring"),sQuery(id+"F4.wireOp",EDGE,"E102.trimOffspring"),sQuery(id+"F4.wireOp",EDGE,"E103.trimOffspring")])],"isStart":true})});
            var sketch = newSketch(context, id + "F11", { "sketchPlane" : qUnion([Q0])});
            skCircle(sketch, "E131", {"center": v(40, -26.5) * mm, "radius": 1.5 * mm});
            skCircle(sketch, "E132", {"center": v(33, -74.5) * mm, "radius": 1.5 * mm});
            skSolve(sketch);
        }
        {
            var Q0;
            Q0 = qSketchRegion(id + "F11", true);
            extrude(context, id + "F12", {"entities" : qUnion([Q0]), "operationType" : NewBodyOperationType.REMOVE, "oppositeDirection" : true, "depth" : 25 * mm, "offsetDistance" : 25 * mm});
        }
    });
